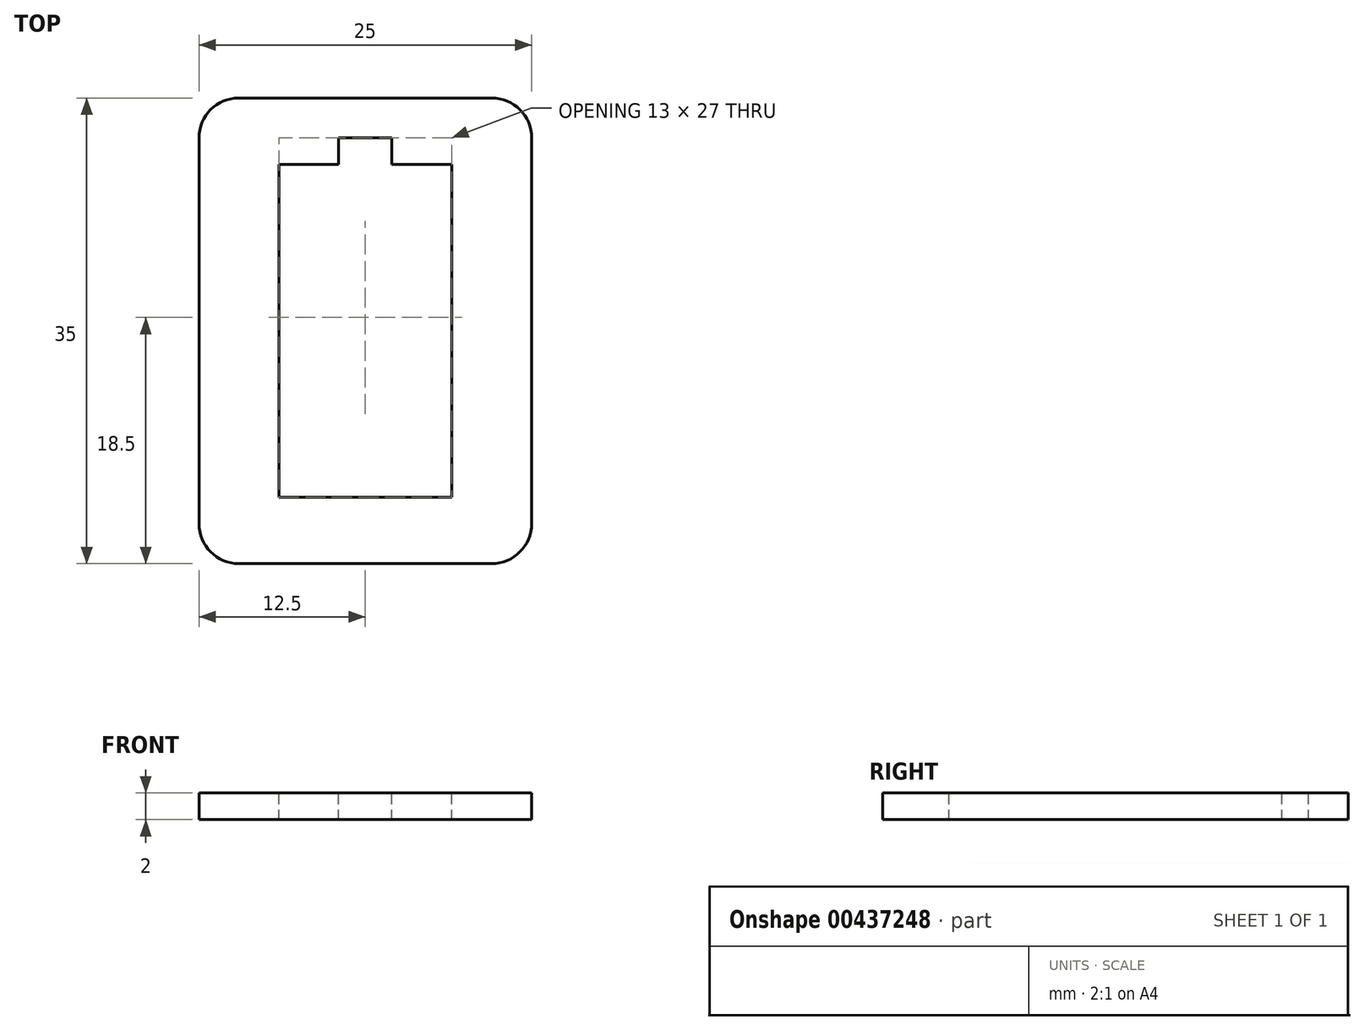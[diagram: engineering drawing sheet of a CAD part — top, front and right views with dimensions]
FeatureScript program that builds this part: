
annotation { "Feature Type Name" : "Feature", "Feature Type Description" : "" }
export const myFeature = defineFeature(function(context is Context, id is Id, definition is map)
    precondition{}
    {
        {
            var Q0;
            Q0=qCreatedBy(makeId("Top.planeOp"),FACE);
            var sketch = newSketch(context, id + "F0", { "sketchPlane" : qUnion([Q0])});
            skLineSegment(sketch, "E0", {"start": v(0, 0) * mm, "end": v(0, 35) * mm});
            skLineSegment(sketch, "E1", {"start": v(0, 35) * mm, "end": v(25, 35) * mm});
            skLineSegment(sketch, "E2", {"start": v(25, 35) * mm, "end": v(25, 0) * mm});
            skLineSegment(sketch, "E3", {"start": v(25, 0) * mm, "end": v(0, 0) * mm});
            skSolve(sketch);
        }
        {
            var Q0;
            Q0=makeQuery(id+"F0.imprint","IMPRINT",FACE,{"disambiguationData":[TD([[makeQuery(id+"F0.imprint","IMPRINT",EDGE,{"derivedFrom":sQuery(id+"F0.wireOp",EDGE,"E0")}),-1.0]])]});
            extrude(context, id + "F1", {"entities" : qUnion([Q0]), "depth" : 2 * mm});
        }
        {
            var Q0;
            Q0=makeQuery(id+"F1.opExtrude","SWEPT_EDGE",EDGE,{"disambiguationData":[OSD([sQuery(id+"F0.wireOp",EDGE,"E1"),sQuery(id+"F0.wireOp",EDGE,"E2")])]});
            var Q1;
            Q1=makeQuery(id+"F1.opExtrude","SWEPT_EDGE",EDGE,{"disambiguationData":[OSD([sQuery(id+"F0.wireOp",EDGE,"E0"),sQuery(id+"F0.wireOp",EDGE,"E1")])]});
            var Q2;
            Q2=makeQuery(id+"F1.opExtrude","SWEPT_EDGE",EDGE,{"disambiguationData":[OSD([sQuery(id+"F0.wireOp",EDGE,"E2"),sQuery(id+"F0.wireOp",EDGE,"E3")])]});
            var Q3;
            Q3=makeQuery(id+"F1.opExtrude","SWEPT_EDGE",EDGE,{"disambiguationData":[OSD([sQuery(id+"F0.wireOp",EDGE,"E0"),sQuery(id+"F0.wireOp",EDGE,"E3")])]});
            fillet(context, id + "F2", {"entities" : qUnion([Q0, Q1, Q2, Q3]), "radius" : 3 * mm, "tangentPropagation" : true, "allowEdgeOverflow" : false});
        }
        {
            var Q0;
            Q0=makeQuery(id+"F1.opExtrude","CAP_FACE",FACE,{"disambiguationData":[OSD([sQuery(id+"F0.wireOp",EDGE,"E0"),sQuery(id+"F0.wireOp",EDGE,"E1"),sQuery(id+"F0.wireOp",EDGE,"E2"),sQuery(id+"F0.wireOp",EDGE,"E3")])],"isStart":false});
            var sketch = newSketch(context, id + "F3", { "sketchPlane" : qUnion([Q0])});
            skLineSegment(sketch, "E4.bottom", {"start": v(6, 30) * mm, "end": v(19, 30) * mm});
            skLineSegment(sketch, "E4.top", {"start": v(6, 5) * mm, "end": v(19, 5) * mm});
            skLineSegment(sketch, "E4.left", {"start": v(6, 30) * mm, "end": v(6, 5) * mm});
            skLineSegment(sketch, "E4.right", {"start": v(19, 30) * mm, "end": v(19, 5) * mm});
            skLineSegment(sketch, "E5.bottom", {"start": v(14.5, 28) * mm, "end": v(10.5, 28) * mm});
            skLineSegment(sketch, "E5.top", {"start": v(14.5, 32) * mm, "end": v(10.5, 32) * mm});
            skLineSegment(sketch, "E5.left", {"start": v(14.5, 28) * mm, "end": v(14.5, 32) * mm});
            skLineSegment(sketch, "E5.right", {"start": v(10.5, 28) * mm, "end": v(10.5, 32) * mm});
            skPoint(sketch, "E5.middle", {"position": v(12.5, 30) * mm});
            skSolve(sketch);
        }
        {
            var Q0;
            Q0=makeQuery(id+"F3.imprint","IMPRINT",FACE,{"disambiguationData":[TD([[makeQuery(id+"F3.imprint","IMPRINT",EDGE,{"derivedFrom":sQuery(id+"F3.wireOp",EDGE,"E4.top")}),1.0]])]});
            var Q1;
            {var subQ5=sQuery(id+"F3.wireOp",EDGE,"E5.top");Q1=makeQuery(id+"F3.imprint","IMPRINT",FACE,{"disambiguationData":[TD([[makeQuery(id+"F3.imprint","IMPRINT",EDGE,{"derivedFrom":subQ5}),1.0]])]});}
            var Q2;
            {var subQ5=sQuery(id+"F3.wireOp",EDGE,"E5.bottom");Q2=makeQuery(id+"F3.imprint","IMPRINT",FACE,{"disambiguationData":[TD([[makeQuery(id+"F3.imprint","IMPRINT",EDGE,{"derivedFrom":subQ5}),-1.0]])]});}
            extrude(context, id + "F4", {"entities" : qUnion([Q0, Q1, Q2]), "operationType" : NewBodyOperationType.REMOVE, "oppositeDirection" : true, "depth" : 100 * mm});
        }
    });
